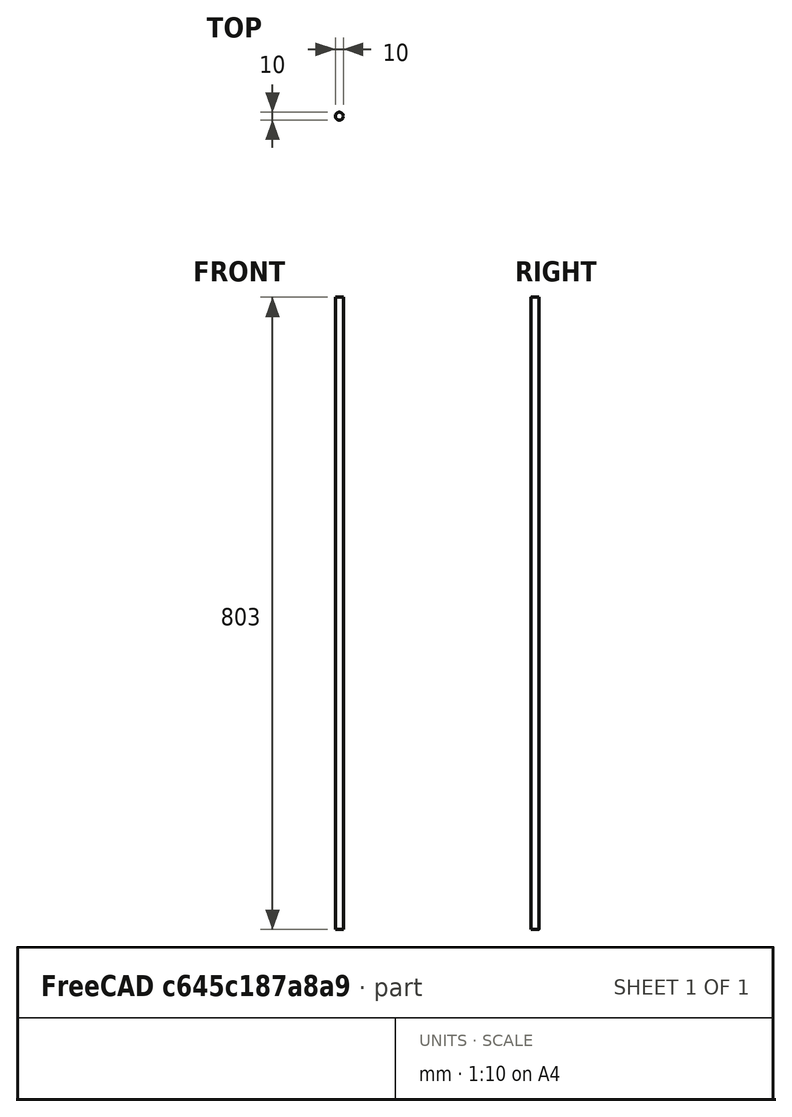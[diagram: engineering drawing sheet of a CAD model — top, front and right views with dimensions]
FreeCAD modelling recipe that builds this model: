
FCSTD DOCUMENT  (FreeCAD 0.14R3702 (Git))
Label: ballscrew_800mm
License: CC-BY 3.0
LicenseURL: http://creativecommons.org/licenses/by/3.0/
objects: Part::Feature×3, Part::Cylinder×2, Part::Cut×2, Sketcher::SketchObject×1, PartDesign::Pad×1
note: 10 computed .brp shape members not serialized (recipe doc carries the construction recipe); baked Part::Feature solids carry a one-line shape summary decoded from their .brp

FEATURE [Sketcher::SketchObject] Sketch
  sketch-geometry (1):
    g0: Circle CenterX=0 CenterY=0 CenterZ=0 NormalX=0 NormalY=0 NormalZ=1 Radius=5
  constraints (2):
    c: Coincident(g0,g-1)
    c: Radius(g0) = 5
FEATURE [PartDesign::Pad] Pad
  Length = 803
  Length2 = 33.15
  Sketch = -> Sketch
  Type = 0
FEATURE [Part::Feature] Sweep
  Placement = pos=(0,-0.000184826,6) rot=(0,0,1;0rad)
  shape: bbox 21.72 x 24.36 x 755 mm, 450 faces, 0 solids (baked)
FEATURE [Part::Cylinder] Cylinder
  Angle = 360
  Height = 11
  Placement = pos=(4.033e-09,-6.65692e-06,0) rot=(0,0,1;0rad)
  Radius = 10
FEATURE [Part::Cut] Cut
  Base = -> Sweep
  Tool = -> Cylinder
FEATURE [Part::Feature] Face
  shape: bbox 15.55 x 14.23 x 2e-07 mm, 1 faces, 0 solids (baked)
FEATURE [Part::Cylinder] Cylinder001
  Angle = 360
  Height = 51
  Placement = pos=(0,0,749) rot=(0,0,1;0rad)
  Radius = 10
FEATURE [Part::Cut] Cut001
  Base = -> Cut
  Tool = -> Cylinder001
FEATURE [Part::Feature] Face001
  shape: bbox 19.81 x 19.02 x 2.002e-07 mm, 1 faces, 0 solids (baked)
